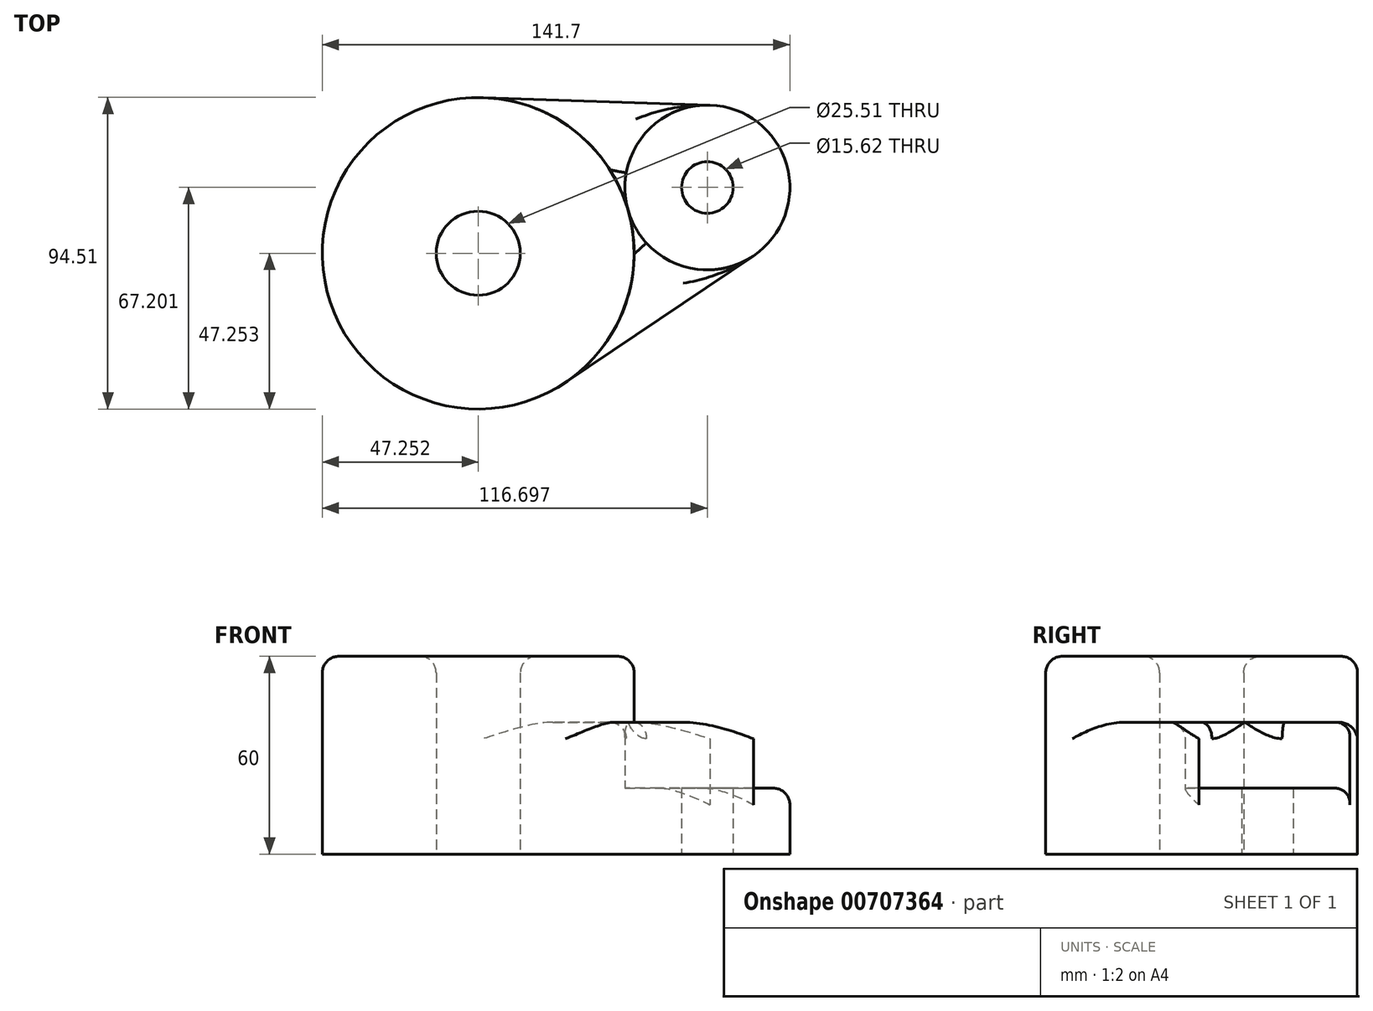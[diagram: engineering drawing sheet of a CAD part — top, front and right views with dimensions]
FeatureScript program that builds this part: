
annotation { "Feature Type Name" : "Feature", "Feature Type Description" : "" }
export const myFeature = defineFeature(function(context is Context, id is Id, definition is map)
    precondition{}
    {
        {
            var Q0;
            Q0=qCreatedBy(makeId("Top.planeOp"),FACE);
            var sketch = newSketch(context, id + "F0", { "sketchPlane" : qUnion([Q0])});
            skCircle(sketch, "E0", {"center": v(-54.83, 9.15) * mm, "radius": 47.25 * mm});
            skCircle(sketch, "E1", {"center": v(14.62, 29.1) * mm, "radius": 7.8 * mm});
            skCircle(sketch, "E2", {"center": v(14.62, 29.1) * mm, "radius": 25 * mm});
            skCircle(sketch, "E3", {"center": v(-54.83, 9.15) * mm, "radius": 12.75 * mm});
            skLineSegment(sketch, "E4", {"start": v(-53.25, 56.38) * mm, "end": v(15.45, 54.09) * mm});
            skLineSegment(sketch, "E5", {"start": v(-28.43, -30.04) * mm, "end": v(28.58, 8.37) * mm});
            skSolve(sketch);
        }
        {
            var Q0;
            Q0=makeQuery(id+"F0.imprint","IMPRINT",FACE,{"disambiguationData":[TD([[makeQuery(id+"F0.imprint","IMPRINT",EDGE,{"derivedFrom":sQuery(id+"F0.wireOp",EDGE,"E3")}),-1.0]])]});
            extrude(context, id + "F1", {"entities" : qUnion([Q0]), "depth" : 60 * mm, "offsetDistance" : 25 * mm});
        }
        {
            var Q0;
            {var subQ0=sQuery(id+"F0.wireOp",EDGE,"E5");Q0=makeQuery(id+"F0.imprint","IMPRINT",FACE,{"disambiguationData":[TD([[makeQuery(id+"F0.imprint","IMPRINT",EDGE,{"derivedFrom":subQ0}),1.0]])]});}
            var Q1;
            {var subQ0=sQuery(id+"F0.wireOp",EDGE,"E4");Q1=makeQuery(id+"F0.imprint","IMPRINT",FACE,{"disambiguationData":[TD([[makeQuery(id+"F0.imprint","IMPRINT",EDGE,{"derivedFrom":subQ0}),-1.0]])]});}
            extrude(context, id + "F2", {"entities" : qUnion([Q0, Q1]), "operationType" : NewBodyOperationType.ADD, "depth" : 40 * mm, "offsetDistance" : 25 * mm});
        }
        {
            var Q0;
            Q0=makeQuery(id+"F0.imprint","IMPRINT",FACE,{"disambiguationData":[TD([[makeQuery(id+"F0.imprint","IMPRINT",EDGE,{"derivedFrom":sQuery(id+"F0.wireOp",EDGE,"E1")}),-1.0]])]});
            extrude(context, id + "F3", {"entities" : qUnion([Q0]), "operationType" : NewBodyOperationType.ADD, "depth" : 20 * mm, "offsetDistance" : 25 * mm});
        }
        {
            var Q0;
            Q0=makeQuery(id+"F1.opExtrude","CAP_FACE",FACE,{"disambiguationData":[OSD([sQuery(id+"F0.wireOp",EDGE,"E0"),sQuery(id+"F0.wireOp",EDGE,"E3")])],"isStart":false});
            var Q1;
            Q1=makeQuery(id+"F2.opExtrude","CAP_EDGE",EDGE,{"disambiguationData":[OSD([sQuery(id+"F0.wireOp",EDGE,"E5")])],"isStart":false});
            var Q2;
            Q2=makeQuery(id+"F2.opExtrude","CAP_EDGE",EDGE,{"disambiguationData":[OSD([sQuery(id+"F0.wireOp",EDGE,"E4")])],"isStart":false});
            var Q3;
            {var subQ0=sQuery(id+"F0.wireOp",EDGE,"E2");Q3=makeQuery(id+"F2.opExtrude","CAP_EDGE",EDGE,{"disambiguationData":[OSD([subQ0]),TDD([makeQuery(id+"F0.imprint","IMPRINT",EDGE,{"disambiguationData":[TD([[makeQuery(id+"F0.imprint","INTERSECT",VERTEX,{"derivedFrom":[subQ0,sQuery(id+"F0.wireOp",EDGE,"E4")]}),-1.0]])],"derivedFrom":subQ0})])],"isStart":false});}
            var Q4;
            {var subQ0=sQuery(id+"F0.wireOp",EDGE,"E2");Q4=makeQuery(id+"F2.opExtrude","CAP_EDGE",EDGE,{"disambiguationData":[OSD([subQ0]),TDD([makeQuery(id+"F0.imprint","IMPRINT",EDGE,{"disambiguationData":[TD([[makeQuery(id+"F0.imprint","INTERSECT",VERTEX,{"derivedFrom":[subQ0,sQuery(id+"F0.wireOp",EDGE,"E5")]}),1.0]])],"derivedFrom":subQ0})])],"isStart":false});}
            var Q5;
            {var subQ0=sQuery(id+"F0.wireOp",EDGE,"E2");Q5=makeQuery(id+"F3.boolean.opBoolean","SPLIT",EDGE,{"disambiguationData":[topologyDisambiguationEdgeConnected([makeQuery(id+"F3.opExtrude","SWEPT_FACE",FACE,{"disambiguationData":[OSD([subQ0])]})])],"derivedFrom":makeQuery(id+"F3.opExtrude","CAP_EDGE",EDGE,{"disambiguationData":[OSD([subQ0])],"isStart":false})});}
            fillet(context, id + "F4", {"entities" : qUnion([Q0, Q1, Q2, Q3, Q4, Q5]), "radius" : 5 * mm, "tangentPropagation" : true, "allowEdgeOverflow" : false});
        }
    });
